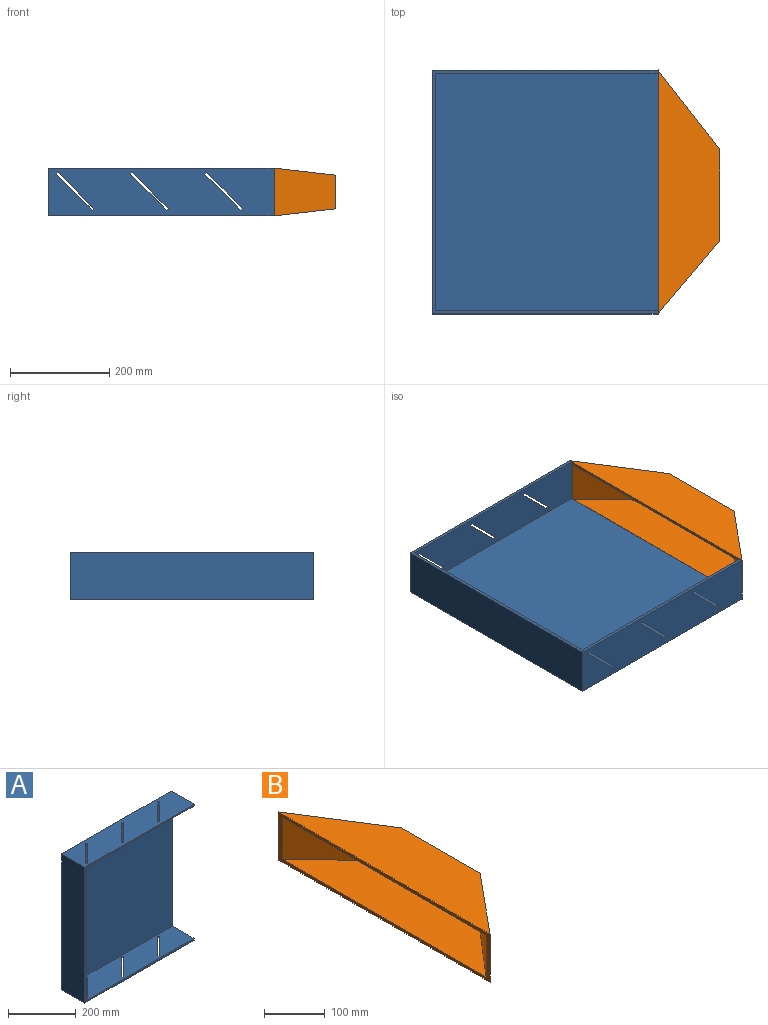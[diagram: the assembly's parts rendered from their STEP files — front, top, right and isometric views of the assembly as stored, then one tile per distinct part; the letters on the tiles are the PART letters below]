
ASSEMBLY  parts=2 mates=1
PART A: 34 faces, bbox 456.4x96.4x492 mm
  f0: plane 456.35x96.35mm, normal (0,0,1), area 42439.3mm2, adj f4,f5,f6,f7,f22,f23,f24,f25
  f1: plane 456.35x96.35mm, normal (0,0,-1), area 42439.3mm2, adj f4,f5,f6,f7,f10,f11,f12,f13
  f2: plane 450.35x90.35mm, normal (0,0,-1), area 39159.1mm2, adj f4,f5,f8,f9,f22,f23,f24,f25
  f3: plane 450.35x90.35mm, normal (0,0,1), area 39159.1mm2, adj f4,f5,f8,f9,f10,f11,f12,f13
  f4: plane 492x96.35mm, normal (1,0,0), area 4036.2mm2, adj f0,f1,f2,f3,f5,f7,f9
  f5: plane 492x456.35mm, normal (0,-1,0), area 8356.2mm2, adj f0,f1,f2,f3,f4,f6,f8
  f6: plane 492x96.35mm, normal (-1,0,0), area 47404.2mm2, adj f0,f1,f5,f7
  f7: plane 492x456.35mm, normal (0,1,0), area 224524.2mm2, adj f0,f1,f4,f6
  f8: plane 480x90.35mm, normal (1,0,0), area 43368mm2, adj f2,f3,f5,f9
  f9: plane 480x450.35mm, normal (0,-1,0), area 216168mm2, adj f2,f3,f4,f8
  f10: plane 6x3.54mm, normal (0.71,0.71,0), area 30mm2, adj f1,f3,f11,f13
  f11: plane 72.13x72.13mm, normal (-0.71,0.71,0), area 612mm2, adj f1,f3,f10,f12
  f12: plane 6x3.54mm, normal (-0.71,-0.71,0), area 30mm2, adj f1,f3,f11,f13
  f13: plane 72.13x72.13mm, normal (0.71,-0.71,0), area 612mm2, adj f1,f3,f10,f12
  f14: plane 6x3.54mm, normal (0.71,0.71,0), area 30mm2, adj f1,f3,f15,f17
  f15: plane 72.13x72.13mm, normal (-0.71,0.71,0), area 612mm2, adj f1,f3,f14,f16
  f16: plane 6x3.54mm, normal (-0.71,-0.71,0), area 30mm2, adj f1,f3,f15,f17
  f17: plane 72.13x72.13mm, normal (0.71,-0.71,0), area 612mm2, adj f1,f3,f14,f16
  f18: plane 72.13x72.13mm, normal (-0.71,0.71,0), area 612mm2, adj f1,f3,f19,f21
  f19: plane 6x3.54mm, normal (-0.71,-0.71,0), area 30mm2, adj f1,f3,f18,f20
  f20: plane 72.13x72.13mm, normal (0.71,-0.71,0), area 612mm2, adj f1,f3,f19,f21
  f21: plane 6x3.54mm, normal (0.71,0.71,0), area 30mm2, adj f1,f3,f18,f20
  f22: plane 72.13x72.13mm, normal (0.71,-0.71,0), area 612mm2, adj f0,f2,f23,f25
  f23: plane 6x3.54mm, normal (-0.71,-0.71,0), area 30mm2, adj f0,f2,f22,f24
  f24: plane 72.13x72.13mm, normal (-0.71,0.71,0), area 612mm2, adj f0,f2,f23,f25
  f25: plane 6x3.54mm, normal (0.71,0.71,0), area 30mm2, adj f0,f2,f22,f24
  f26: plane 72.13x72.13mm, normal (0.71,-0.71,0), area 612mm2, adj f0,f2,f27,f29
  f27: plane 6x3.54mm, normal (-0.71,-0.71,0), area 30mm2, adj f0,f2,f26,f28
  f28: plane 72.13x72.13mm, normal (-0.71,0.71,0), area 612mm2, adj f0,f2,f27,f29
  f29: plane 6x3.54mm, normal (0.71,0.71,0), area 30mm2, adj f0,f2,f26,f28
  f30: plane 6x3.54mm, normal (0.71,0.71,0), area 30mm2, adj f0,f2,f31,f33
  f31: plane 72.13x72.13mm, normal (0.71,-0.71,0), area 612mm2, adj f0,f2,f30,f32
  f32: plane 6x3.54mm, normal (-0.71,-0.71,0), area 30mm2, adj f0,f2,f31,f33
  f33: plane 72.13x72.13mm, normal (-0.71,0.71,0), area 612mm2, adj f0,f2,f30,f32
PART B: 10 faces, bbox 125x492.7x96.3 mm
  f0: plane 183.63x67.82mm, normal (1,0,0), area 3281.6mm2, adj f2,f3,f4,f5,f6,f7,f8,f9
  f1: plane 492.7x96.3mm, normal (-1,0,0), area 7558mm2, adj f2,f3,f4,f5,f6,f7,f8,f9
  f2: plane 147.92x125mm, normal (0.76,-0.65,0), area 15891.4mm2, adj f0,f1,f3,f5
  f3: plane 492.7x125mm, normal (0.11,0,-0.99), area 42544.3mm2, adj f0,f1,f2,f4
  f4: plane 161.15x125mm, normal (0.79,0.61,0), area 16735.4mm2, adj f0,f1,f3,f5
  f5: plane 492.7x125mm, normal (0.11,0,0.99), area 42544.3mm2, adj f0,f1,f2,f4
  f6: plane 147.92x125mm, normal (-0.76,0.65,0), area 13552.5mm2, adj f0,f1,f7,f9
  f7: plane 473.62x125mm, normal (-0.11,0,0.99), area 40143.2mm2, adj f0,f1,f6,f8
  f8: plane 161.15x125mm, normal (-0.79,-0.61,0), area 14272.2mm2, adj f0,f1,f7,f9
  f9: plane 473.62x125mm, normal (-0.11,0,-0.99), area 40143.2mm2, adj f0,f1,f6,f8
PLACE A rot(axis=(-1,0,0),90deg) t=(261.57,116.97,82.91)mm
PLACE B t=(25.57,-62.84,85.83)mm
MATE parallel A.f4 <-> B.f1  axis (1,0,0) through (25.57,66.97,37.61)mm
